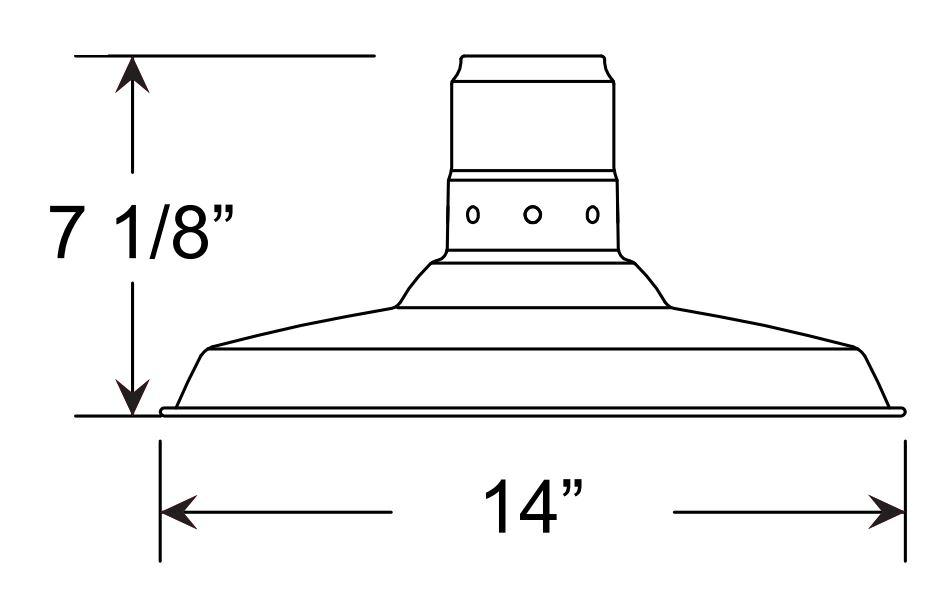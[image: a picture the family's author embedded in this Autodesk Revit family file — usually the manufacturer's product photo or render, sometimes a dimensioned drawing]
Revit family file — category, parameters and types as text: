
# Revit family: MILKCAN F(8,10,12,18)MB
name_source: partatom
category: Lighting Fixtures
units: mm (PartAtom-declared; Revit-internal decimal feet)

## family parameters
Always vertical = Yes
Cut with Voids When Loaded = No
Light Source = Yes
OmniClass Number = 23.80.70.00
OmniClass Title = Lighting
Part Type = Normal
Room Calculation Point = No
Round Connector Dimension = Use Diameter
Shared = No
Work Plane-Based = No

## types (4) — shared parameters
Body Colour = Spun aluminium
Body Material = body
CRI = >90
Color Filter = 16777215
Construction Material = Heavy Duty spun aluminum.
Default Elevation = 0' - 0"
Description = 120-277 Voltage
Dimming = 1%
Dimming Lamp Color Temperature Shift = <None>
Efficiency = 65-125 lumens per watt
Lamp = MB
Life = L70 50,000 hours
Load Classification = Lighting
Manufacturer = ANP Lighting
Photometric Web File = generic.ies
Power Factor = 1
Tilt Angle = 90.00°
URL = https://www.anplighting.com
Voltage = 277 V
Warranty = 5 year limited warranty

## per-type parameters (varying)
| type | Apparent Load | Fixture Diameter | Fixture Height | MCF08 | MCF10 | MCF12 | MCF18 | Wattage Comments | Weight |
| MCF08 | 100 VA | 0' - 8" | 0' - 4" | Yes | No | No | No | 100W Max | 1 lbs |
| MCF10 | 100 VA | 0' - 10" | 0' - 4" | No | Yes | No | No | 100W Max | 1 lbs |
| MCF12 | 200 VA | 1' - 0" | 0' - 5" | No | No | Yes | No | 200W Max | 1.5 lbs |
| MCF18 | 200 VA | 0' - 6" | 1' - 6" | No | No | No | Yes | 200W Max | 2 lbs |

note: column(s) folded — value = type name in every type: Model

## geometry (parser evidence)
native form markers: Sweep x35
no freeform markers — native parametric forms only
